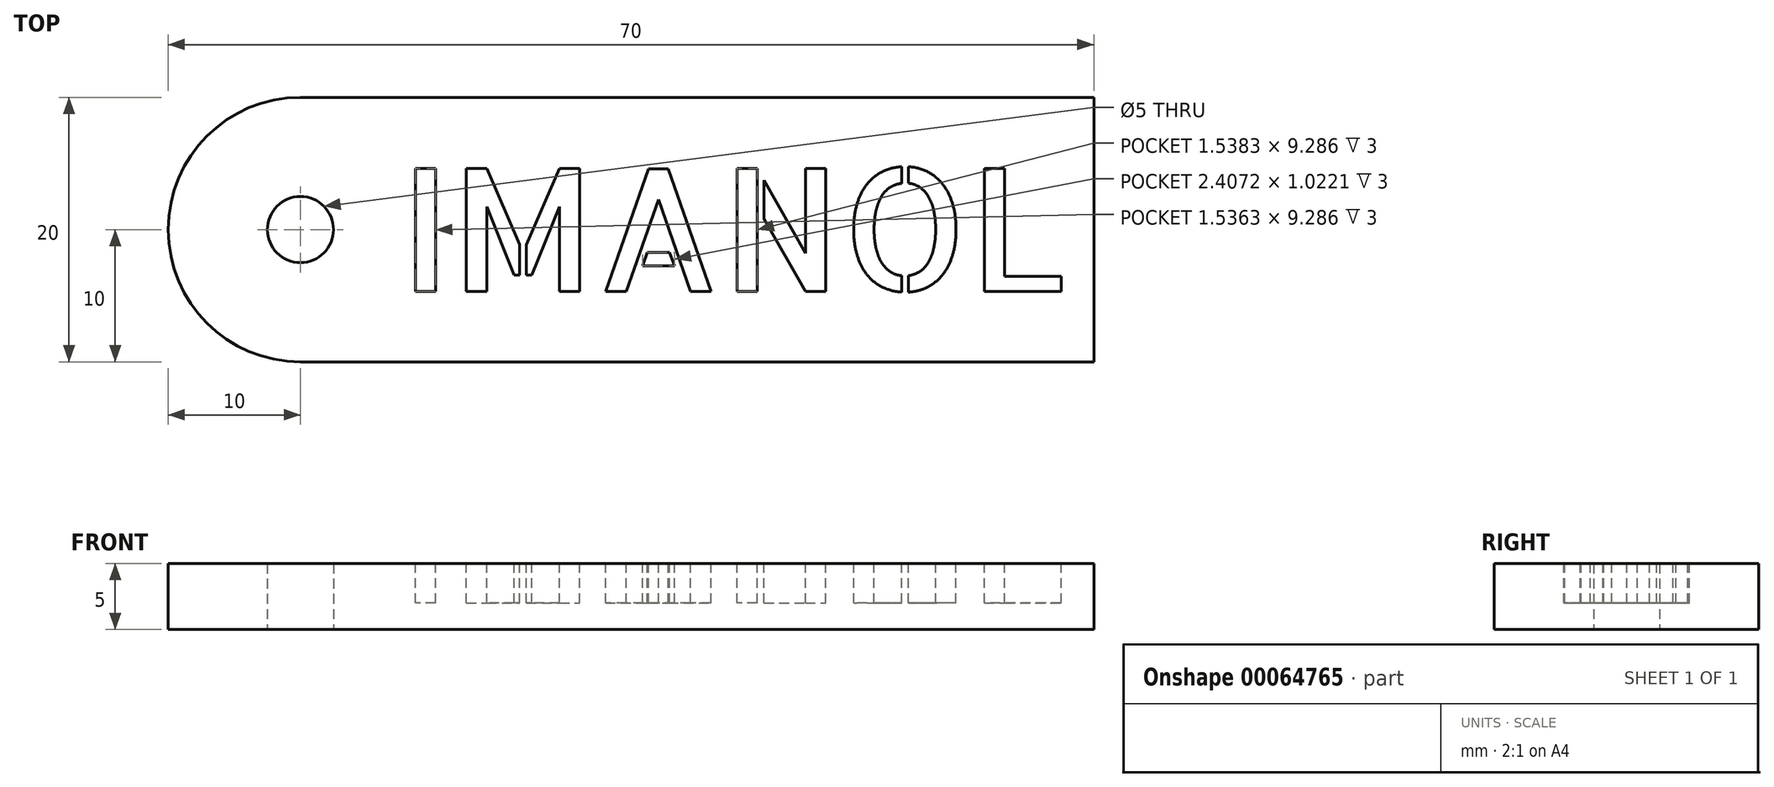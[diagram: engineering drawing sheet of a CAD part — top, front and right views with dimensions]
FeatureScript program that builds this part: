
annotation { "Feature Type Name" : "Feature", "Feature Type Description" : "" }
export const myFeature = defineFeature(function(context is Context, id is Id, definition is map)
    precondition{}
    {
        {
            var Q0;
            Q0=qCreatedBy(makeId("Top.planeOp"),FACE);
            var sketch = newSketch(context, id + "F0", { "sketchPlane" : qUnion([Q0])});
            skLineSegment(sketch, "E0.rect.bottom", {"start": v(30, 10) * mm, "end": v(-30, 10) * mm});
            skLineSegment(sketch, "E0.rect.top", {"start": v(30, -10) * mm, "end": v(-30, -10) * mm});
            skLineSegment(sketch, "E0.rect.left", {"start": v(30, 10) * mm, "end": v(30, -10) * mm});
            skPoint(sketch, "E0.rect.middle", {"position": v(0, 0) * mm});
            skArc(sketch, "E1", {"start": v(-30, 10) * mm, "mid": v(-40, 0) * mm, "end": v(-30, -10) * mm});
            skCircle(sketch, "E2", {"center": v(-30, 0) * mm, "radius": 2.5 * mm});
            skSolve(sketch);
        }
        {
            var Q0;
            Q0 = qSketchRegion(id + "F0", true);
            extrude(context, id + "F1", {"entities" : qUnion([Q0]), "depth" : 5 * mm});
        }
        {
            var Q0;
            Q0=makeQuery(id+"F1.opExtrude","CAP_FACE",FACE,{"disambiguationData":[OSD([sQuery(id+"F0.wireOp",EDGE,"E0.rect.bottom"),sQuery(id+"F0.wireOp",EDGE,"E0.rect.top"),sQuery(id+"F0.wireOp",EDGE,"E0.rect.left"),sQuery(id+"F0.wireOp",EDGE,"E1"),sQuery(id+"F0.wireOp",EDGE,"E2")])],"isStart":false});
            var sketch = newSketch(context, id + "F2", { "sketchPlane" : qUnion([Q0])});
            skSolve(sketch);
        }
        {
            var Q0;
            Q0=makeQuery(id+"F2.imprint","IMPRINT",FACE,{"disambiguationData":[TD([[makeQuery(id+"F2.imprint","IMPRINT",EDGE,{"derivedFrom":makeQuery(id+"F1.opExtrude","CAP_EDGE",EDGE,{"disambiguationData":[OSD([sQuery(id+"F0.wireOp",EDGE,"E0.rect.bottom")])],"isStart":false})}),1.0]])]});
            var sketch = newSketch(context, id + "F3", { "sketchPlane" : qUnion([Q0])});
            skText(sketch, "E3", { "text": "IMANOL", "fontName": "AllertaStencil-Regular.ttf"});
            const initialGuessF3  = {"E3": [-0.0225, -0.00467, 1, 0, 0.00929]};
            skSetInitialGuess(sketch, initialGuessF3);
            skSolve(sketch);
        }
        {
            var Q0;
            Q0 = qSketchRegion(id + "F3", true);
            extrude(context, id + "F4", {"entities" : qUnion([Q0]), "operationType" : NewBodyOperationType.REMOVE, "oppositeDirection" : true, "depth" : 3 * mm});
        }
    });
